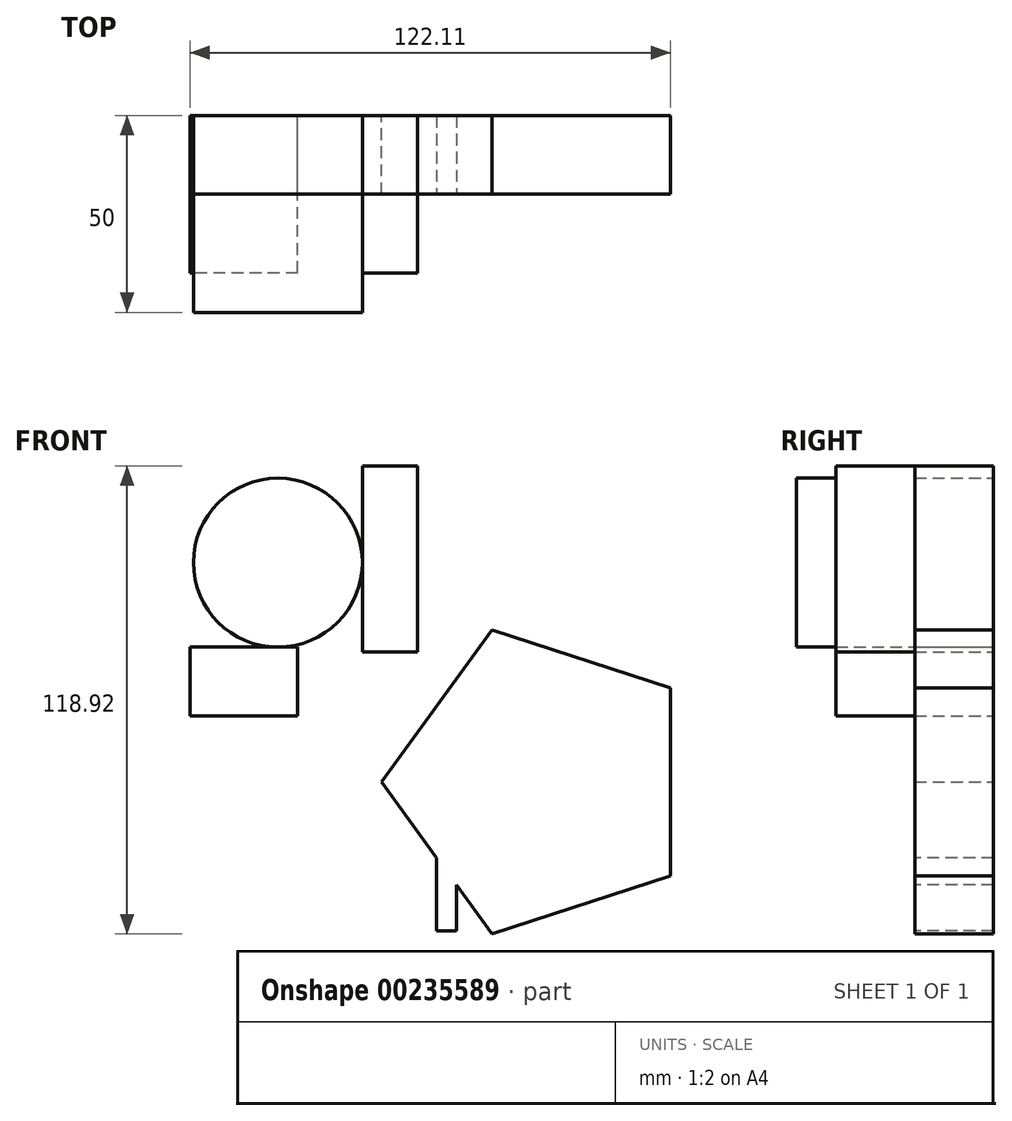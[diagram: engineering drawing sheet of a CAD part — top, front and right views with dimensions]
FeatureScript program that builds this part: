
annotation { "Feature Type Name" : "Feature", "Feature Type Description" : "" }
export const myFeature = defineFeature(function(context is Context, id is Id, definition is map)
    precondition{}
    {
        {
            var Q0;
            Q0=qCreatedBy(makeId("Front.planeOp"),FACE);
            var sketch = newSketch(context, id + "F0", { "sketchPlane" : qUnion([Q0])});
            skCircle(sketch, "E0", {"center": v(-40.36, 22.68) * mm, "radius": 21.46 * mm});
            skLineSegment(sketch, "E1.bottom", {"start": v(-18.9, 0) * mm, "end": v(-4.9, 0) * mm});
            skLineSegment(sketch, "E1.top", {"start": v(-18.9, 47.25) * mm, "end": v(-4.9, 47.25) * mm});
            skLineSegment(sketch, "E1.left", {"start": v(-18.9, 0) * mm, "end": v(-18.9, 47.25) * mm});
            skLineSegment(sketch, "E1.right", {"start": v(-4.9, 0) * mm, "end": v(-4.9, 47.25) * mm});
            skPoint(sketch, "E1.middle", {"position": v(-11.9, 23.63) * mm});
            skLineSegment(sketch, "E2.bottom", {"start": v(-35.33, -16.28) * mm, "end": v(-62.68, -16.28) * mm});
            skLineSegment(sketch, "E2.top", {"start": v(-35.33, 1.23) * mm, "end": v(-62.68, 1.23) * mm});
            skLineSegment(sketch, "E2.left", {"start": v(-35.33, -16.28) * mm, "end": v(-35.33, 1.23) * mm});
            skLineSegment(sketch, "E2.right", {"start": v(-62.68, -16.28) * mm, "end": v(-62.68, 1.23) * mm});
            skPoint(sketch, "E2.middle", {"position": v(-49, -7.53) * mm});
            skCircle(sketch, "E3.cCircle", {"center": v(26.6, -33.08) * mm, "radius": 32.83 * mm, "construction": true});
            skLineSegment(sketch, "E3.0", {"start": v(59.43, -9.23) * mm, "end": v(59.43, -56.93) * mm});
            skLineSegment(sketch, "E3.1", {"start": v(59.43, -56.93) * mm, "end": v(14.06, -71.67) * mm});
            skLineSegment(sketch, "E3.2", {"start": v(14.06, -71.67) * mm, "end": v(-13.98, -33.08) * mm});
            skLineSegment(sketch, "E3.3", {"start": v(-13.98, -33.08) * mm, "end": v(14.06, 5.51) * mm});
            skLineSegment(sketch, "E3.4", {"start": v(14.06, 5.51) * mm, "end": v(59.43, -9.23) * mm});
            skPoint(sketch, "E3.0.midPoint", {"position": v(59.43, -33.08) * mm});
            skSolve(sketch);
        }
        {
            var Q0;
            {var subQ3=sQuery(id+"F0.wireOp",EDGE,"E1.bottom");Q0=makeQuery(id+"F0.imprint","IMPRINT",FACE,{"disambiguationData":[TD([[makeQuery(id+"F0.imprint","IMPRINT",EDGE,{"derivedFrom":subQ3}),1.0]])]});}
            var Q1;
            Q1=makeQuery(id+"F0.imprint","IMPRINT",FACE,{"disambiguationData":[TD([[makeQuery(id+"F0.imprint","IMPRINT",EDGE,{"derivedFrom":sQuery(id+"F0.wireOp",EDGE,"E2.bottom")}),-1.0]])]});
            extrude(context, id + "F1", {"entities" : qUnion([Q0, Q1]), "depth" : 40 * mm});
        }
        {
            var Q0;
            {var subQ0=sQuery(id+"F0.wireOp",EDGE,"E0");var subQ1=makeQuery(id+"F0.imprint","INTERSECT",VERTEX,{"derivedFrom":[subQ0,sQuery(id+"F0.wireOp",EDGE,"E1.left")]});Q0=makeQuery(id+"F0.imprint","IMPRINT",FACE,{"disambiguationData":[TD([[makeQuery(id+"F0.imprint","IMPRINT",EDGE,{"disambiguationData":[TD([[subQ1,-1.0]])],"derivedFrom":subQ0}),1.0]])]});}
            extrude(context, id + "F2", {"entities" : qUnion([Q0]), "depth" : 50 * mm});
        }
        {
            var Q0;
            {var subQ0=sQuery(id+"F0.wireOp",EDGE,"E0");var subQ1=makeQuery(id+"F0.imprint","INTERSECT",VERTEX,{"derivedFrom":[subQ0,sQuery(id+"F0.wireOp",EDGE,"E1.left")]});Q0=makeQuery(id+"F0.imprint","IMPRINT",FACE,{"disambiguationData":[TD([[makeQuery(id+"F0.imprint","IMPRINT",EDGE,{"disambiguationData":[TD([[subQ1,-1.0]])],"derivedFrom":subQ0}),1.0]])]});}
            var Q1;
            {var subQ3=sQuery(id+"F0.wireOp",EDGE,"E1.bottom");Q1=makeQuery(id+"F0.imprint","IMPRINT",FACE,{"disambiguationData":[TD([[makeQuery(id+"F0.imprint","IMPRINT",EDGE,{"derivedFrom":subQ3}),1.0]])]});}
            var Q2;
            Q2=makeQuery(id+"F0.imprint","IMPRINT",FACE,{"disambiguationData":[TD([[makeQuery(id+"F0.imprint","IMPRINT",EDGE,{"derivedFrom":sQuery(id+"F0.wireOp",EDGE,"E2.bottom")}),-1.0]])]});
            var Q3;
            Q3=makeQuery(id+"F0.imprint","IMPRINT",FACE,{"disambiguationData":[TD([[makeQuery(id+"F0.imprint","IMPRINT",EDGE,{"derivedFrom":sQuery(id+"F0.wireOp",EDGE,"E3.0")}),-1.0]])]});
            extrude(context, id + "F3", {"entities" : qUnion([Q0, Q1, Q2, Q3]), "depth" : 20 * mm});
        }
        {
            var Q0;
            Q0=qCreatedBy(makeId("Right.planeOp"),FACE);
            var sketch = newSketch(context, id + "F4", { "sketchPlane" : qUnion([Q0])});
            skLineSegment(sketch, "E4.bottom", {"start": v(0, -16.03) * mm, "end": v(-20, -16.03) * mm});
            skLineSegment(sketch, "E4.top", {"start": v(0, -70.86) * mm, "end": v(-20, -70.86) * mm});
            skLineSegment(sketch, "E4.left", {"start": v(0, -16.03) * mm, "end": v(0, -70.86) * mm});
            skLineSegment(sketch, "E4.right", {"start": v(-20, -16.03) * mm, "end": v(-20, -70.86) * mm});
            skSolve(sketch);
        }
        {
            var Q0;
            Q0=makeQuery(id+"F4.imprint","IMPRINT",FACE,{"disambiguationData":[TD([[makeQuery(id+"F4.imprint","IMPRINT",EDGE,{"derivedFrom":sQuery(id+"F4.wireOp",EDGE,"E4.bottom")}),1.0]])]});
            extrude(context, id + "F5", {"entities" : qUnion([Q0]), "operationType" : NewBodyOperationType.ADD, "depth" : 5 * mm});
        }
    });
